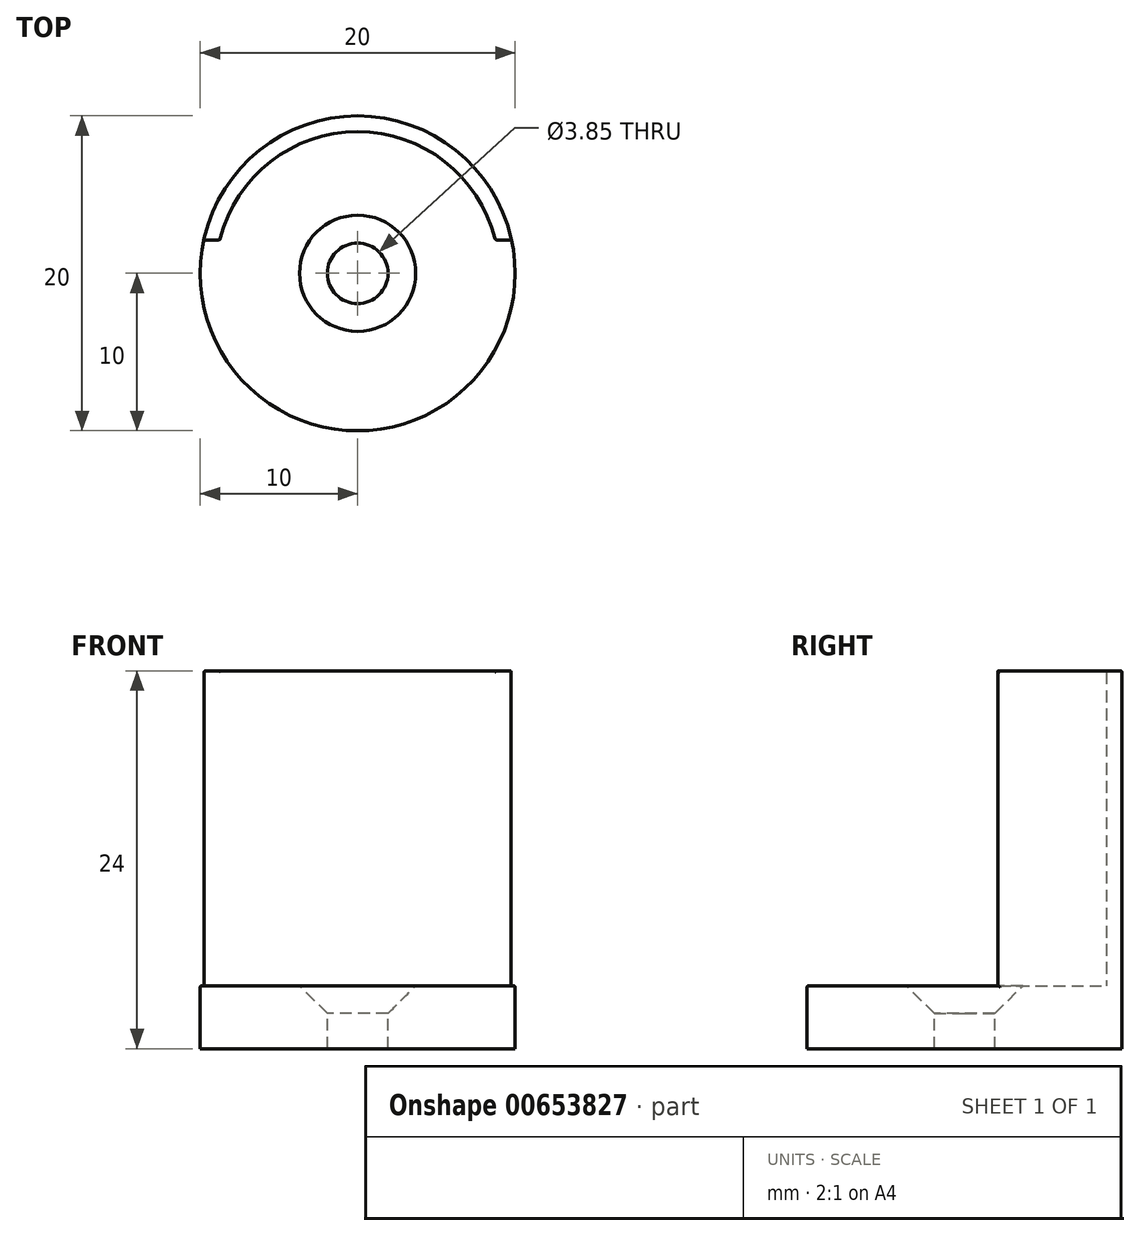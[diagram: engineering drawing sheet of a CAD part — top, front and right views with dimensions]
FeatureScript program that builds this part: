
annotation { "Feature Type Name" : "Feature", "Feature Type Description" : "" }
export const myFeature = defineFeature(function(context is Context, id is Id, definition is map)
    precondition{}
    {
        {
            var Q0;
            Q0=qCreatedBy(makeId("Top.planeOp"),FACE);
            var sketch = newSketch(context, id + "F0", { "sketchPlane" : qUnion([Q0])});
            skCircle(sketch, "E0", {"center": v(0, 0) * mm, "radius": 10 * mm});
            skCircle(sketch, "E1", {"center": v(0, 0) * mm, "radius": 9 * mm});
            skLineSegment(sketch, "E2", {"start": v(-9.77, 2.12) * mm, "end": v(9.77, 2.12) * mm});
            skSolve(sketch);
        }
        {
            var Q0;
            {var subQ0=sQuery(id+"F0.wireOp",EDGE,"E2");var subQ1=sQuery(id+"F0.wireOp",EDGE,"E0");var subQ2=makeQuery(id+"F0.imprint","INTERSECT",VERTEX,{"disambiguationData":[OD(0.0)],"derivedFrom":[subQ1,subQ0]});Q0=makeQuery(id+"F0.imprint","IMPRINT",FACE,{"disambiguationData":[TD([[makeQuery(id+"F0.imprint","IMPRINT",EDGE,{"disambiguationData":[TD([[subQ2,-1.0]])],"derivedFrom":subQ1}),1.0]])]});}
            extrude(context, id + "F1", {"entities" : qUnion([Q0]), "depth" : 20 * mm, "offsetDistance" : 25 * mm});
        }
        {
            var Q0;
            {var subQ0=sQuery(id+"F0.wireOp",EDGE,"E2");var subQ1=sQuery(id+"F0.wireOp",EDGE,"E1");var subQ2=makeQuery(id+"F0.imprint","INTERSECT",VERTEX,{"disambiguationData":[OD(0.0)],"derivedFrom":[subQ1,subQ0]});Q0=makeQuery(id+"F0.imprint","IMPRINT",FACE,{"disambiguationData":[TD([[makeQuery(id+"F0.imprint","IMPRINT",EDGE,{"disambiguationData":[TD([[subQ2,1.0]])],"derivedFrom":subQ1}),1.0]])]});}
            var Q1;
            {var subQ0=sQuery(id+"F0.wireOp",EDGE,"E2");var subQ1=sQuery(id+"F0.wireOp",EDGE,"E0");var subQ2=makeQuery(id+"F0.imprint","INTERSECT",VERTEX,{"disambiguationData":[OD(0.0)],"derivedFrom":[subQ1,subQ0]});Q1=makeQuery(id+"F0.imprint","IMPRINT",FACE,{"disambiguationData":[TD([[makeQuery(id+"F0.imprint","IMPRINT",EDGE,{"disambiguationData":[TD([[subQ2,1.0]])],"derivedFrom":subQ1}),1.0]])]});}
            var Q2;
            {var subQ0=sQuery(id+"F0.wireOp",EDGE,"E2");var subQ1=sQuery(id+"F0.wireOp",EDGE,"E0");var subQ2=makeQuery(id+"F0.imprint","INTERSECT",VERTEX,{"disambiguationData":[OD(0.0)],"derivedFrom":[subQ1,subQ0]});Q2=makeQuery(id+"F0.imprint","IMPRINT",FACE,{"disambiguationData":[TD([[makeQuery(id+"F0.imprint","IMPRINT",EDGE,{"disambiguationData":[TD([[subQ2,-1.0]])],"derivedFrom":subQ1}),1.0]])]});}
            var Q3;
            {var subQ0=sQuery(id+"F0.wireOp",EDGE,"E2");var subQ1=sQuery(id+"F0.wireOp",EDGE,"E1");var subQ2=makeQuery(id+"F0.imprint","INTERSECT",VERTEX,{"disambiguationData":[OD(0.0)],"derivedFrom":[subQ1,subQ0]});Q3=makeQuery(id+"F0.imprint","IMPRINT",FACE,{"disambiguationData":[TD([[makeQuery(id+"F0.imprint","IMPRINT",EDGE,{"disambiguationData":[TD([[subQ2,-1.0]])],"derivedFrom":subQ1}),1.0]])]});}
            extrude(context, id + "F2", {"entities" : qUnion([Q0, Q1, Q2, Q3]), "operationType" : NewBodyOperationType.ADD, "oppositeDirection" : true, "depth" : 4 * mm, "offsetDistance" : 25 * mm});
        }
        {
            var Q0;
            {var subQ0=sQuery(id+"F0.wireOp",EDGE,"E2");var subQ1=sQuery(id+"F0.wireOp",EDGE,"E0");Q0=makeQuery(id+"F1.opExtrude","SWEPT_EDGE",EDGE,{"disambiguationData":[OSD([subQ1,subQ0]),TDD([makeQuery(id+"F0.imprint","INTERSECT",VERTEX,{"disambiguationData":[OD(1.0)],"derivedFrom":[subQ1,subQ0]})])]});}
            var Q1;
            {var subQ0=sQuery(id+"F0.wireOp",EDGE,"E2");var subQ1=sQuery(id+"F0.wireOp",EDGE,"E1");Q1=makeQuery(id+"F1.opExtrude","SWEPT_EDGE",EDGE,{"disambiguationData":[OSD([subQ1,subQ0]),TDD([makeQuery(id+"F0.imprint","INTERSECT",VERTEX,{"disambiguationData":[OD(1.0)],"derivedFrom":[subQ1,subQ0]})])]});}
            var Q2;
            {var subQ0=sQuery(id+"F0.wireOp",EDGE,"E2");var subQ1=sQuery(id+"F0.wireOp",EDGE,"E1");Q2=makeQuery(id+"F1.opExtrude","SWEPT_EDGE",EDGE,{"disambiguationData":[OSD([subQ1,subQ0]),TDD([makeQuery(id+"F0.imprint","INTERSECT",VERTEX,{"disambiguationData":[OD(0.0)],"derivedFrom":[subQ1,subQ0]})])]});}
            var Q3;
            {var subQ0=sQuery(id+"F0.wireOp",EDGE,"E2");var subQ1=sQuery(id+"F0.wireOp",EDGE,"E0");Q3=makeQuery(id+"F1.opExtrude","SWEPT_EDGE",EDGE,{"disambiguationData":[OSD([subQ1,subQ0]),TDD([makeQuery(id+"F0.imprint","INTERSECT",VERTEX,{"disambiguationData":[OD(0.0)],"derivedFrom":[subQ1,subQ0]})])]});}
            var Q4;
            Q4=makeQuery(id+"F1.opExtrude","CAP_EDGE",EDGE,{"disambiguationData":[OSD([sQuery(id+"F0.wireOp",EDGE,"E0")])],"isStart":false});
            var Q5;
            Q5=makeQuery(id+"F1.opExtrude","CAP_EDGE",EDGE,{"disambiguationData":[OSD([sQuery(id+"F0.wireOp",EDGE,"E1")])],"isStart":false});
            fillet(context, id + "F3", {"entities" : qUnion([Q0, Q1, Q2, Q3, Q4, Q5]), "radius" : 0.1 * mm, "tangentPropagation" : true, "allowEdgeOverflow" : false});
        }
        {
            var Q0;
            Q0=makeQuery(id+"F2.opExtrude","CAP_EDGE",EDGE,{"disambiguationData":[OSD([sQuery(id+"F0.wireOp",EDGE,"E0")])],"isStart":true});
            fillet(context, id + "F4", {"entities" : qUnion([Q0]), "radius" : 0.1 * mm, "tangentPropagation" : true, "allowEdgeOverflow" : false});
        }
        {
            var Q0;
            Q0=makeQuery(id+"F2.opExtrude","CAP_FACE",FACE,{"disambiguationData":[OSD([sQuery(id+"F0.wireOp",EDGE,"E0")])],"isStart":true});
            var sketch = newSketch(context, id + "F5", { "sketchPlane" : qUnion([Q0])});
            skCircle(sketch, "E3", {"center": v(0, 0) * mm, "radius": 1.38 * mm});
            skSolve(sketch);
        }
        {
            var Q0;
            Q0=sQuery(id+"F5.wireOp",VERTEX,"E3.center");
            var Q1;
            Q1=makeQuery(id+"F1.opExtrude","SWEPT_BODY",BODY,{"disambiguationData":[OSD([sQuery(id+"F0.wireOp",EDGE,"E0"),sQuery(id+"F0.wireOp",EDGE,"E1"),sQuery(id+"F0.wireOp",EDGE,"E2")])]});
            hole(context, id + "F6", {"style" : HoleStyle.C_SINK, "endStyle" : HoleEndStyle.THROUGH, "holeDiameter" : 3.85 * mm, "cSinkDiameter" : 7.38 * mm, "cSinkAngle" : 90 * degree, "majorDiameter" : 5 * mm, "isTappedThrough" : true, "tappedDepth" : 12 * mm, "tapClearance" : 3, "locations" : qUnion([Q0]), "scope" : qUnion([Q1])});
        }
    });
